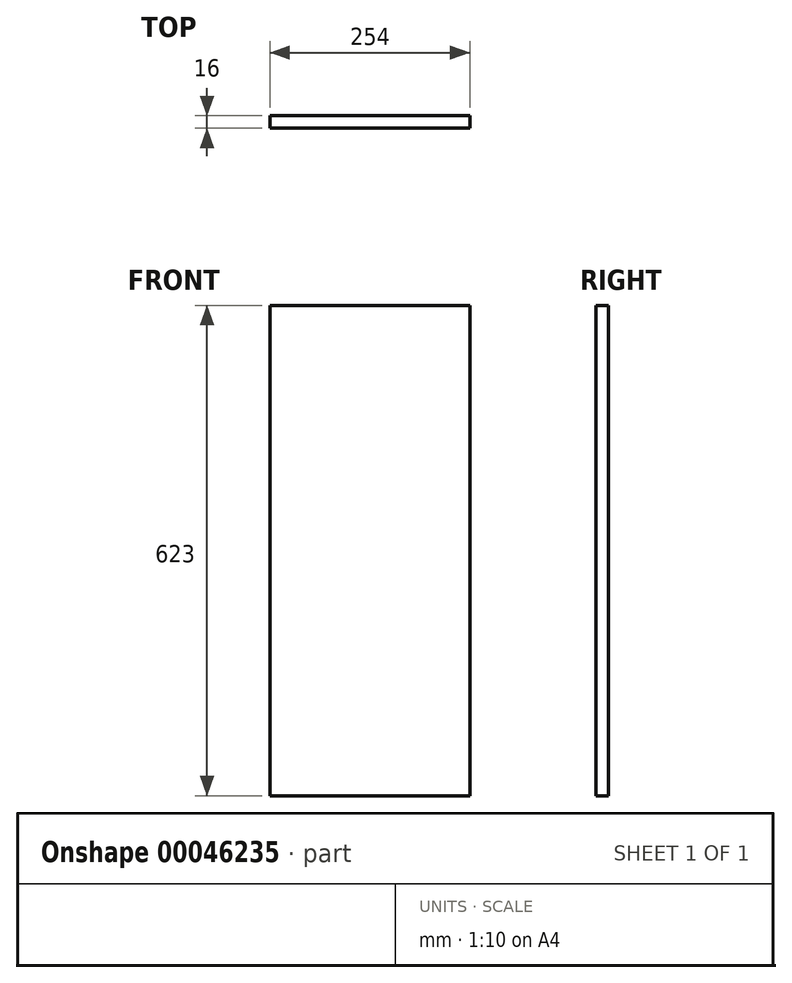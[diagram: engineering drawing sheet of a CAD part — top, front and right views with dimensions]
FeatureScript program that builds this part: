
annotation { "Feature Type Name" : "Feature", "Feature Type Description" : "" }
export const myFeature = defineFeature(function(context is Context, id is Id, definition is map)
    precondition{}
    {
        {
            var Q0;
            Q0=qCreatedBy(makeId("Front.planeOp"),FACE);
            var sketch = newSketch(context, id + "F0", { "sketchPlane" : qUnion([Q0])});
            skLineSegment(sketch, "E0.rect.bottom", {"start": v(127, 311.5) * mm, "end": v(-127, 311.5) * mm});
            skLineSegment(sketch, "E0.rect.top", {"start": v(127, -311.5) * mm, "end": v(-127, -311.5) * mm});
            skLineSegment(sketch, "E0.rect.left", {"start": v(127, 311.5) * mm, "end": v(127, -311.5) * mm});
            skLineSegment(sketch, "E0.rect.right", {"start": v(-127, 311.5) * mm, "end": v(-127, -311.5) * mm});
            skPoint(sketch, "E0.rect.middle", {"position": v(0, 0) * mm});
            skSolve(sketch);
        }
        {
            var Q0;
            Q0 = qSketchRegion(id + "F0", true);
            extrude(context, id + "F1", {"entities" : qUnion([Q0]), "depth" : 16 * mm});
        }
    });
